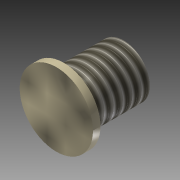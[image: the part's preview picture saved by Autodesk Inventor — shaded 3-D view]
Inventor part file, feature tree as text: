
AUTODESK INVENTOR PART (.ipt)
format: ipt  version: 2015 (Build 190159000, 159)  size: 96,768 bytes
history: native  units: in
note: dims shown in document units (in); Inventor stores cm internally (conversion verified against a paired STEP export)
features: extrude x2, sketch x2, thread x1
ambient origin geometry x8: Origin, YZ Plane, XZ Plane, XY Plane, X Axis, Y Axis, Z Axis, Center Point
bodies: Solid1 (feature_tree)
feature tree (5):
  extrude  "Extrusion1"  Depth=0.05in TaperAngle=0.0deg
  extrude  "Extrusion2"  Depth=0.4in TaperAngle=0.0deg
  thread  "Thread1"  [1 undecoded]
  sketch  "Sketch1"  dims[d0=0.49in d1=0.05in d2=0.0in]
  sketch  "Sketch2"  dims[d3=0.35in d4=0.4in d5=0.0in d6=1.0in d7=0.0in]
note: 1 required parameter value undecoded (feature->parameter linkage not recoverable at this tier; creation-order binding heuristic only, values carry confidence <= 0.55)
